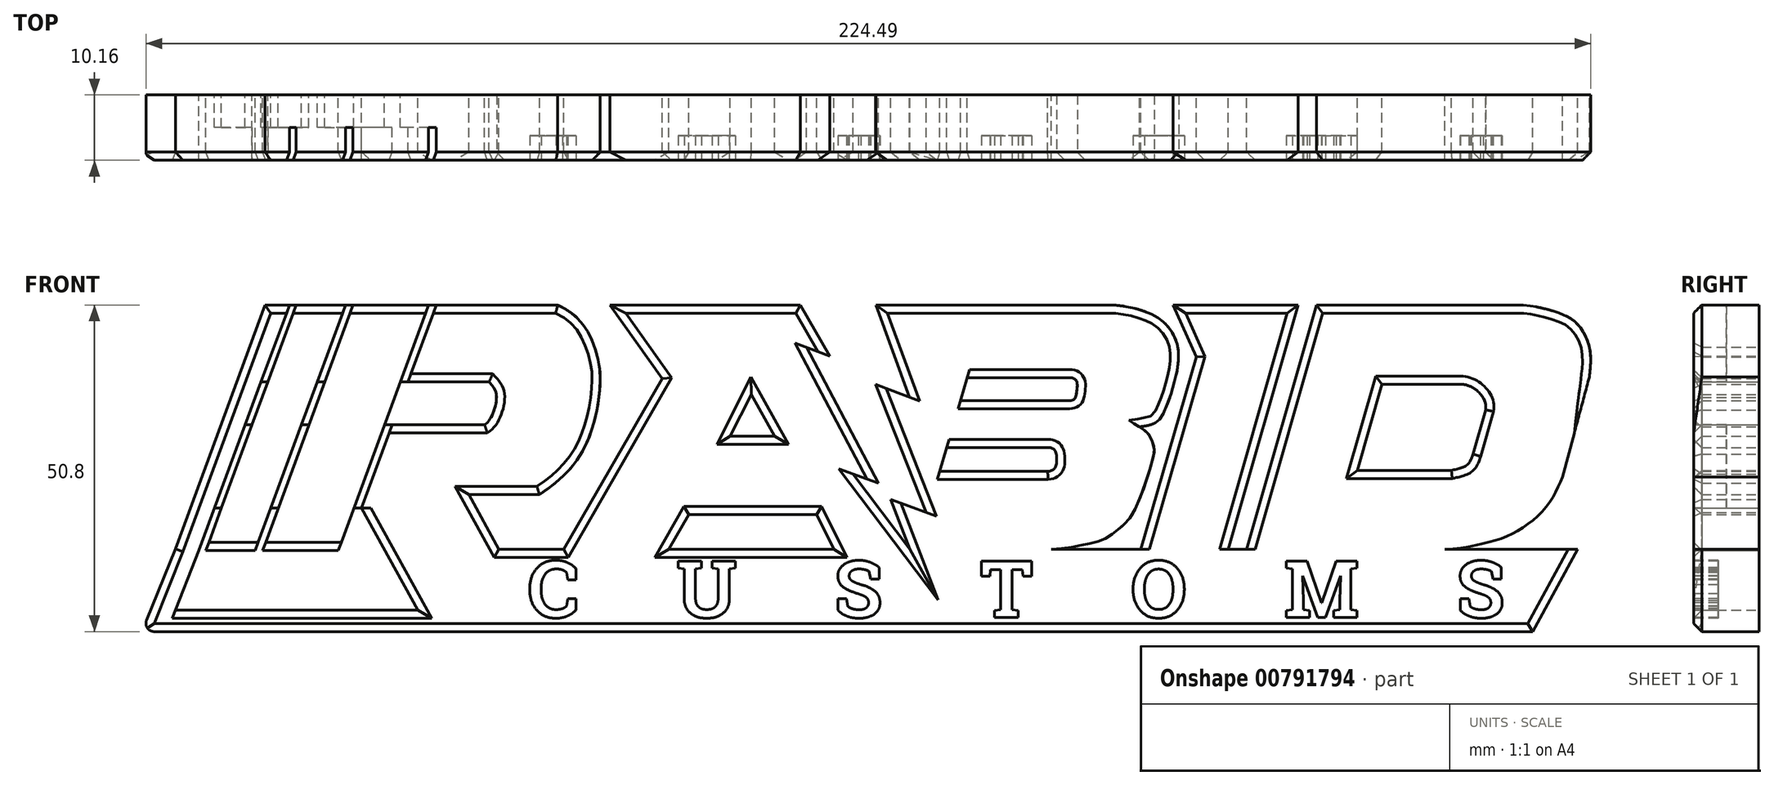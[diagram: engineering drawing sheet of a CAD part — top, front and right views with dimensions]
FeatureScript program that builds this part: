
annotation { "Feature Type Name" : "Feature", "Feature Type Description" : "" }
export const myFeature = defineFeature(function(context is Context, id is Id, definition is map)
    precondition{}
    {
        {
            var Q0;
            Q0=qCreatedBy(makeId("Front.planeOp"),FACE);
            var sketch = newSketch(context, id + "F0", { "sketchPlane" : qUnion([Q0])});
            skLineSegment(sketch, "E0", {"start": v(44.45, 18.23) * mm, "end": v(13.33, 18.23) * mm});
            skLineSegment(sketch, "E1", {"start": v(-163.98, -19.69) * mm, "end": v(-150.03, 18.23) * mm});
            skLineSegment(sketch, "E2", {"start": v(-138.67, -19.93) * mm, "end": v(-150.42, -19.93) * mm});
            skLineSegment(sketch, "E3", {"start": v(-150.69, 6.26) * mm, "end": v(-153.14, -0.4) * mm});
            skLineSegment(sketch, "E4", {"start": v(-159.23, -19.93) * mm, "end": v(-156.81, -13.36) * mm});
            skLineSegment(sketch, "E5", {"start": v(-141.94, 6.26) * mm, "end": v(-144.39, -0.4) * mm});
            skLineSegment(sketch, "E6", {"start": v(-150.42, -19.93) * mm, "end": v(-148, -13.36) * mm});
            skLineSegment(sketch, "E7", {"start": v(-129.04, 6.26) * mm, "end": v(-131.49, -0.4) * mm});
            skLineSegment(sketch, "E8", {"start": v(-127.97, 6.26) * mm, "end": v(-115.24, 6.26) * mm});
            skLineSegment(sketch, "E9", {"start": v(-115.92, -0.4) * mm, "end": v(-130.28, -0.4) * mm});
            skLineSegment(sketch, "E10", {"start": v(-135.05, -13.36) * mm, "end": v(-126.3, -29.24) * mm});
            skLineSegment(sketch, "E11", {"start": v(-124.47, -32.57) * mm, "end": v(-110.55, -32.57) * mm});
            skLineSegment(sketch, "E12", {"start": v(-110.55, -32.57) * mm, "end": v(-103.65, -19.74) * mm});
            skLineSegment(sketch, "E13", {"start": v(-103.65, -19.74) * mm, "end": v(-113.7, -19.74) * mm});
            skLineSegment(sketch, "E14", {"start": v(-113.7, -19.74) * mm, "end": v(-118.36, -11.28) * mm});
            skLineSegment(sketch, "E15", {"start": v(-118.36, -11.28) * mm, "end": v(-107.38, -11.28) * mm});
            skLineSegment(sketch, "E16", {"start": v(-103.65, -19.74) * mm, "end": v(-87.29, -19.74) * mm});
            skLineSegment(sketch, "E17", {"start": v(-96.42, 18.23) * mm, "end": v(-88.35, 6.81) * mm});
            skLineSegment(sketch, "E18", {"start": v(-88.35, 6.81) * mm, "end": v(-103.65, -19.74) * mm});
            skLineSegment(sketch, "E19", {"start": v(-87.29, -19.74) * mm, "end": v(-84.2, -14.4) * mm});
            skLineSegment(sketch, "E20", {"start": v(-84.2, -14.4) * mm, "end": v(-64.33, -14.4) * mm});
            skLineSegment(sketch, "E21", {"start": v(-64.33, -14.4) * mm, "end": v(-61.66, -19.74) * mm});
            skLineSegment(sketch, "E22", {"start": v(-66.84, 18.23) * mm, "end": v(-62.3, 10.3) * mm});
            skLineSegment(sketch, "E23", {"start": v(-62.3, 10.3) * mm, "end": v(-65.92, 11.65) * mm});
            skLineSegment(sketch, "E24", {"start": v(-65.92, 11.65) * mm, "end": v(-54.7, -9.5) * mm});
            skLineSegment(sketch, "E25", {"start": v(-54.7, -9.5) * mm, "end": v(-58.68, -8.06) * mm});
            skLineSegment(sketch, "E26", {"start": v(-58.68, -8.06) * mm, "end": v(-49.86, -19.74) * mm});
            skLineSegment(sketch, "E27", {"start": v(-70.89, -2.18) * mm, "end": v(-77.76, -2.18) * mm});
            skLineSegment(sketch, "E28", {"start": v(-77.76, -2.18) * mm, "end": v(-74.5, 4.32) * mm});
            skLineSegment(sketch, "E29", {"start": v(-74.5, 4.32) * mm, "end": v(-70.89, -2.18) * mm});
            skLineSegment(sketch, "E30", {"start": v(-55.14, 18.23) * mm, "end": v(-49.92, 3.87) * mm});
            skLineSegment(sketch, "E31", {"start": v(-49.92, 3.87) * mm, "end": v(-55.16, 5.86) * mm});
            skLineSegment(sketch, "E32", {"start": v(-55.16, 5.86) * mm, "end": v(-47.3, -14.02) * mm});
            skLineSegment(sketch, "E33", {"start": v(-47.3, -14.02) * mm, "end": v(-52.8, -12.04) * mm});
            skLineSegment(sketch, "E34", {"start": v(-52.8, -12.04) * mm, "end": v(-49.86, -19.74) * mm});
            skLineSegment(sketch, "E35", {"start": v(-40.97, 6.88) * mm, "end": v(-42, 3.36) * mm});
            skLineSegment(sketch, "E36", {"start": v(-45.2, -7.65) * mm, "end": v(-28.43, -7.65) * mm});
            skLineSegment(sketch, "E37", {"start": v(-44.14, -3.97) * mm, "end": v(-28.03, -3.97) * mm});
            skLineSegment(sketch, "E38", {"start": v(-40.97, 6.88) * mm, "end": v(-24.6, 6.88) * mm});
            skLineSegment(sketch, "E39", {"start": v(-42, 3.36) * mm, "end": v(-25, 3.36) * mm});
            skLineSegment(sketch, "E40", {"start": v(-8.93, 18.23) * mm, "end": v(-5.34, 10.12) * mm});
            skLineSegment(sketch, "E41", {"start": v(-5.34, 10.12) * mm, "end": v(-13.99, -19.74) * mm});
            skLineSegment(sketch, "E42", {"start": v(10.46, 18.23) * mm, "end": v(-0.4, -19.74) * mm});
            skLineSegment(sketch, "E43", {"start": v(13.33, 18.23) * mm, "end": v(2.47, -19.74) * mm});
            skLineSegment(sketch, "E44", {"start": v(35.81, 5.9) * mm, "end": v(23.48, 5.9) * mm});
            skLineSegment(sketch, "E45", {"start": v(23.48, 5.9) * mm, "end": v(19.66, -7.49) * mm});
            skLineSegment(sketch, "E46", {"start": v(19.66, -7.49) * mm, "end": v(34.3, -7.49) * mm});
            skLineSegment(sketch, "E47", {"start": v(39.6, 1.92) * mm, "end": v(37.65, -4.94) * mm});
            skFitSpline(sketch, "E48", {"points": [v(55.73, 7.05) * mm, v(55.73, 11.7) * mm, v(53.74, 15.4) * mm, v(50.9, 17) * mm, v(44.45, 18.23) * mm], "startDerivative": vector(2.3, 18.78) * mm, "endDerivative": vector(-24.45, 0) * mm});
            skLineSegment(sketch, "E49", {"start": v(55.73, 7.05) * mm, "end": v(51.56, -8.5) * mm});
            skFitSpline(sketch, "E50", {"points": [v(-14.17, -0.73) * mm, v(-12.02, -0.26) * mm, v(-10.54, 1.23) * mm, v(-8.14, 9.39) * mm, v(-8.72, 13.21) * mm, v(-10.35, 15.5) * mm, v(-13.7, 17.35) * mm, v(-18.93, 18.23) * mm], "startDerivative": vector(20.2, 3.41) * mm, "endDerivative": vector(-28.09, 0) * mm});
            skFitSpline(sketch, "E51", {"points": [v(-14.17, -0.73) * mm, v(-12.8, -1.84) * mm, v(-11.95, -3.81) * mm, v(-12.1, -5.72) * mm, v(-14.99, -13.75) * mm, v(-17.24, -16.5) * mm, v(-19.85, -18.27) * mm, v(-23.1, -19.11) * mm, v(-27.89, -19.74) * mm], "startDerivative": vector(16.43, -10.07) * mm, "endDerivative": vector(-33.98, 0) * mm});
            skFitSpline(sketch, "E52", {"points": [v(-24.6, 6.88) * mm, v(-24.2, 6.68) * mm, v(-23.87, 6.14) * mm, v(-24.05, 4.06) * mm, v(-24.29, 3.61) * mm, v(-25, 3.36) * mm], "startDerivative": vector(3.09, 0) * mm, "endDerivative": vector(-4.49, 0) * mm});
            skFitSpline(sketch, "E53", {"points": [v(-28.03, -3.97) * mm, v(-27.5, -4.2) * mm, v(-27.12, -4.85) * mm, v(-27.1, -6.65) * mm, v(-27.44, -7.25) * mm, v(-28.43, -7.65) * mm], "startDerivative": vector(3.73, 0) * mm, "endDerivative": vector(-8.7, -0.89) * mm});
            skFitSpline(sketch, "E54", {"points": [v(-104.57, 18.23) * mm, v(-101.7, 16.39) * mm, v(-99.55, 13.37) * mm, v(-98.04, 8.28) * mm, v(-98.33, 2.83) * mm, v(-99.98, -3.05) * mm, v(-103.2, -7.86) * mm, v(-107.38, -11.28) * mm], "startDerivative": vector(25.95, -13.02) * mm, "endDerivative": vector(-29.28, -21.25) * mm});
            skFitSpline(sketch, "E55", {"points": [v(35.81, 5.9) * mm, v(37.17, 5.6) * mm, v(38.23, 4.97) * mm, v(39.07, 4.03) * mm, v(39.6, 1.92) * mm], "startDerivative": vector(5.58, 0) * mm, "endDerivative": vector(-1.33, -10.82) * mm});
            skFitSpline(sketch, "E56", {"points": [v(34.3, -7.49) * mm, v(35.48, -7.2) * mm, v(36.57, -6.77) * mm, v(37.26, -5.96) * mm, v(37.65, -4.94) * mm], "startDerivative": vector(4.57, 1.01) * mm, "endDerivative": vector(1.33, 4.26) * mm});
            skLineSegment(sketch, "E57.trimOffspring", {"start": v(-146.28, 18.23) * mm, "end": v(-150.03, 18.23) * mm});
            skLineSegment(sketch, "E58.trimOffspring", {"start": v(-137.53, 18.23) * mm, "end": v(-145.19, 18.23) * mm});
            skLineSegment(sketch, "E59.trimOffspring", {"start": v(-124.63, 18.23) * mm, "end": v(-136.37, 18.23) * mm});
            skLineSegment(sketch, "E60.trimOffspring", {"start": v(-104.57, 18.23) * mm, "end": v(-123.56, 18.23) * mm});
            skLineSegment(sketch, "E61.trimOffspring", {"start": v(-151.57, -19.93) * mm, "end": v(-159.23, -19.93) * mm});
            skLineSegment(sketch, "E62.trimOffspring", {"start": v(-61.66, -19.74) * mm, "end": v(-49.86, -19.74) * mm});
            skLineSegment(sketch, "E63.trimOffspring", {"start": v(-49.86, -19.74) * mm, "end": v(-27.89, -19.74) * mm});
            skLineSegment(sketch, "E64.trimOffspring", {"start": v(-66.84, 18.23) * mm, "end": v(-96.42, 18.23) * mm});
            skLineSegment(sketch, "E65.trimOffspring", {"start": v(-44.14, -3.97) * mm, "end": v(-45.2, -7.65) * mm});
            skLineSegment(sketch, "E66.trimOffspring", {"start": v(-18.93, 18.23) * mm, "end": v(-55.14, 18.23) * mm});
            skLineSegment(sketch, "E67.trimOffspring", {"start": v(-13.99, -19.74) * mm, "end": v(-0.4, -19.74) * mm});
            skLineSegment(sketch, "E68.trimOffspring", {"start": v(2.47, -19.74) * mm, "end": v(33.3, -19.74) * mm});
            skLineSegment(sketch, "E69.trimOffspring", {"start": v(10.46, 18.23) * mm, "end": v(-8.93, 18.23) * mm});
            skFitSpline(sketch, "E70", {"points": [v(51.56, -8.5) * mm, v(50.36, -11.15) * mm, v(48.41, -13.9) * mm, v(45.57, -16.27) * mm, v(42.49, -17.92) * mm, v(38.84, -18.97) * mm, v(33.3, -19.74) * mm], "startDerivative": vector(-7.47, -18.05) * mm, "endDerivative": vector(-28.9, 0) * mm});
            skFitSpline(sketch, "E71", {"points": [v(-115.24, 6.26) * mm, v(-114.2, 4.72) * mm, v(-114.26, 2.54) * mm, v(-115.24, 0.25) * mm, v(-115.92, -0.4) * mm], "startDerivative": vector(5.02, -5.67) * mm, "endDerivative": vector(-3.78, -2.78) * mm});
            skLineSegment(sketch, "E72", {"start": v(-87.29, -19.74) * mm, "end": v(-61.66, -19.74) * mm});
            skLineSegment(sketch, "E73", {"start": v(-27.89, -19.74) * mm, "end": v(-13.99, -19.74) * mm});
            skLineSegment(sketch, "E74", {"start": v(-0.4, -19.74) * mm, "end": v(2.47, -19.74) * mm});
            skLineSegment(sketch, "E75", {"start": v(27.98, -32.57) * mm, "end": v(-110.55, -32.57) * mm});
            skLineSegment(sketch, "E76", {"start": v(27.98, -32.57) * mm, "end": v(46.92, -32.57) * mm});
            skLineSegment(sketch, "E77", {"start": v(46.92, -32.57) * mm, "end": v(53.92, -19.74) * mm});
            skLineSegment(sketch, "E78", {"start": v(33.3, -19.74) * mm, "end": v(53.92, -19.74) * mm});
            skLineSegment(sketch, "E79", {"start": v(-123.56, 18.23) * mm, "end": v(-124.63, 18.23) * mm});
            skLineSegment(sketch, "E80", {"start": v(-136.37, 18.23) * mm, "end": v(-137.53, 18.23) * mm});
            skLineSegment(sketch, "E81", {"start": v(-127.97, 6.26) * mm, "end": v(-129.04, 6.26) * mm});
            skLineSegment(sketch, "E82", {"start": v(-130.28, -0.4) * mm, "end": v(-131.49, -0.4) * mm});
            skLineSegment(sketch, "E83", {"start": v(-145.19, 18.23) * mm, "end": v(-146.28, 18.23) * mm});
            skLineSegment(sketch, "E84", {"start": v(-140.78, 6.26) * mm, "end": v(-141.94, 6.26) * mm});
            skLineSegment(sketch, "E85", {"start": v(-149.6, 6.26) * mm, "end": v(-150.69, 6.26) * mm});
            skLineSegment(sketch, "E86", {"start": v(-143.23, -0.4) * mm, "end": v(-144.39, -0.4) * mm});
            skLineSegment(sketch, "E87", {"start": v(-152.05, -0.4) * mm, "end": v(-153.14, -0.4) * mm});
            skLineSegment(sketch, "E88", {"start": v(-135.05, -13.36) * mm, "end": v(-136.25, -13.36) * mm});
            skLineSegment(sketch, "E89", {"start": v(-148, -13.36) * mm, "end": v(-149.15, -13.36) * mm});
            skLineSegment(sketch, "E90", {"start": v(-156.81, -13.36) * mm, "end": v(-157.9, -13.36) * mm});
            skLineSegment(sketch, "E91", {"start": v(-163.98, -19.69) * mm, "end": v(-168.88, -31.87) * mm});
            skLineSegment(sketch, "E92", {"start": v(-168.4, -32.57) * mm, "end": v(-124.47, -32.57) * mm});
            skLineSegment(sketch, "E93", {"start": v(-160.32, -19.93) * mm, "end": v(-163.98, -29.24) * mm});
            skLineSegment(sketch, "E94", {"start": v(-163.98, -29.24) * mm, "end": v(-126.3, -29.24) * mm});
            skLineSegment(sketch, "E95.trimOffspring", {"start": v(-152.05, -0.4) * mm, "end": v(-149.6, 6.26) * mm});
            skLineSegment(sketch, "E96.trimOffspring", {"start": v(-157.9, -13.36) * mm, "end": v(-160.32, -19.93) * mm});
            skLineSegment(sketch, "E97.trimOffspring", {"start": v(-149.15, -13.36) * mm, "end": v(-151.57, -19.93) * mm});
            skLineSegment(sketch, "E98.trimOffspring", {"start": v(-143.23, -0.4) * mm, "end": v(-140.78, 6.26) * mm});
            skLineSegment(sketch, "E99.trimOffspring", {"start": v(-136.25, -13.36) * mm, "end": v(-138.67, -19.93) * mm});
            skLineSegment(sketch, "E100", {"start": v(-168.88, -31.87) * mm, "end": v(-169.16, -32.57) * mm});
            skLineSegment(sketch, "E101", {"start": v(-169.16, -32.57) * mm, "end": v(-168.4, -32.57) * mm});
            skSolve(sketch);
        }
        {
            var Q0;
            Q0=qSketchRegion(id+"F0",true);
            extrude(context, id + "F1", {"entities" : qUnion([Q0]), "depth" : 10.16 * mm, "offsetDistance" : 25.4 * mm});
        }
        {
            var Q0;
            {var subQ0=sQuery(id+"F0.wireOp",EDGE,"E28");var subQ1=sQuery(id+"F0.wireOp",EDGE,"E27");var subQ2=sQuery(id+"F0.wireOp",EDGE,"E25");var subQ3=sQuery(id+"F0.wireOp",EDGE,"E22");var subQ4=sQuery(id+"F0.wireOp",EDGE,"E21");var subQ5=sQuery(id+"F0.wireOp",EDGE,"E20");var subQ6=sQuery(id+"F0.wireOp",EDGE,"E19");var subQ7=sQuery(id+"F0.wireOp",EDGE,"E18");var subQ8=sQuery(id+"F0.wireOp",EDGE,"E17");var subQ9=sQuery(id+"F0.wireOp",EDGE,"E15");var subQ10=sQuery(id+"F0.wireOp",EDGE,"E14");var subQ11=sQuery(id+"F0.wireOp",EDGE,"E13");var subQ12=sQuery(id+"F0.wireOp",EDGE,"E76");var subQ13=sQuery(id+"F0.wireOp",EDGE,"E75");var subQ14=sQuery(id+"F0.wireOp",EDGE,"E11");var subQ15=sQuery(id+"F0.wireOp",EDGE,"E10");var subQ16=sQuery(id+"F0.wireOp",EDGE,"E82");var subQ17=sQuery(id+"F0.wireOp",EDGE,"E9");var subQ18=sQuery(id+"F0.wireOp",EDGE,"E81");var subQ19=sQuery(id+"F0.wireOp",EDGE,"E8");var subQ20=sQuery(id+"F0.wireOp",EDGE,"E7");var subQ21=sQuery(id+"F0.wireOp",EDGE,"E2");var subQ22=sQuery(id+"F0.wireOp",EDGE,"E88");var subQ23=sQuery(id+"F0.wireOp",EDGE,"E84");var subQ24=sQuery(id+"F0.wireOp",EDGE,"E6");var subQ25=sQuery(id+"F0.wireOp",EDGE,"E86");var subQ26=sQuery(id+"F0.wireOp",EDGE,"E89");var subQ27=sQuery(id+"F0.wireOp",EDGE,"E61.trimOffspring");var subQ28=sQuery(id+"F0.wireOp",EDGE,"E5");var subQ29=sQuery(id+"F0.wireOp",EDGE,"E85");var subQ30=sQuery(id+"F0.wireOp",EDGE,"E4");var subQ31=sQuery(id+"F0.wireOp",EDGE,"E87");var subQ32=sQuery(id+"F0.wireOp",EDGE,"E90");var subQ33=sQuery(id+"F0.wireOp",EDGE,"f4ebd289-e4e5-4d37-ab03-dc2c71f6bb5f.trimOffspring");var subQ34=sQuery(id+"F0.wireOp",EDGE,"E3");var subQ35=sQuery(id+"F0.wireOp",EDGE,"E1");var subQ36=sQuery(id+"F0.wireOp",EDGE,"E0");var subQ37=sQuery(id+"F0.wireOp",EDGE,"E78");var subQ38=sQuery(id+"F0.wireOp",EDGE,"E77");var subQ39=sQuery(id+"F0.wireOp",EDGE,"E73");var subQ40=sQuery(id+"F0.wireOp",EDGE,"E72");var subQ41=sQuery(id+"F0.wireOp",EDGE,"E71");var subQ42=sQuery(id+"F0.wireOp",EDGE,"E70");var subQ43=sQuery(id+"F0.wireOp",EDGE,"E69.trimOffspring");var subQ44=sQuery(id+"F0.wireOp",EDGE,"E66.trimOffspring");var subQ45=sQuery(id+"F0.wireOp",EDGE,"E65.trimOffspring");var subQ46=sQuery(id+"F0.wireOp",EDGE,"E46");var subQ47=sQuery(id+"F0.wireOp",EDGE,"E74");var subQ48=sQuery(id+"F0.wireOp",EDGE,"E45");var subQ49=sQuery(id+"F0.wireOp",EDGE,"E43");var subQ50=sQuery(id+"F0.wireOp",EDGE,"E48");var subQ51=sQuery(id+"F0.wireOp",EDGE,"E26");var subQ52=sQuery(id+"F0.wireOp",EDGE,"E47");var subQ53=sQuery(id+"F0.wireOp",EDGE,"E44");var subQ54=sQuery(id+"F0.wireOp",EDGE,"E53");var subQ55=sQuery(id+"F0.wireOp",EDGE,"E39");var subQ56=sQuery(id+"F0.wireOp",EDGE,"E38");var subQ57=sQuery(id+"F0.wireOp",EDGE,"E30");var subQ58=sQuery(id+"F0.wireOp",EDGE,"E29");var subQ59=sQuery(id+"F0.wireOp",EDGE,"E31");var subQ60=sQuery(id+"F0.wireOp",EDGE,"E49");var subQ61=sQuery(id+"F0.wireOp",EDGE,"E42");var subQ62=sQuery(id+"F0.wireOp",EDGE,"E37");var subQ63=sQuery(id+"F0.wireOp",EDGE,"E32");var subQ64=sQuery(id+"F0.wireOp",EDGE,"E33");var subQ65=sQuery(id+"F0.wireOp",EDGE,"E34");var subQ66=sQuery(id+"F0.wireOp",EDGE,"E35");var subQ67=sQuery(id+"F0.wireOp",EDGE,"E36");var subQ68=sQuery(id+"F0.wireOp",EDGE,"E50");var subQ69=sQuery(id+"F0.wireOp",EDGE,"E51");var subQ70=sQuery(id+"F0.wireOp",EDGE,"E52");var subQ71=sQuery(id+"F0.wireOp",EDGE,"E54");var subQ72=sQuery(id+"F0.wireOp",EDGE,"E23");var subQ73=sQuery(id+"F0.wireOp",EDGE,"E55");var subQ74=sQuery(id+"F0.wireOp",EDGE,"E24");var subQ75=sQuery(id+"F0.wireOp",EDGE,"E56");var subQ76=sQuery(id+"F0.wireOp",EDGE,"E83");var subQ77=sQuery(id+"F0.wireOp",EDGE,"E80");var subQ78=sQuery(id+"F0.wireOp",EDGE,"E79");var subQ79=sQuery(id+"F0.wireOp",EDGE,"E60.trimOffspring");var subQ80=sQuery(id+"F0.wireOp",EDGE,"E59.trimOffspring");var subQ81=sQuery(id+"F0.wireOp",EDGE,"E58.trimOffspring");var subQ82=sQuery(id+"F0.wireOp",EDGE,"E57.trimOffspring");var subQ83=sQuery(id+"F0.wireOp",EDGE,"E64.trimOffspring");var subQ84=sQuery(id+"F0.wireOp",EDGE,"E40");var subQ85=sQuery(id+"F0.wireOp",EDGE,"E41");Q0=makeQuery(id+"F5.boolean.opBoolean","SPLIT",FACE,{"disambiguationData":[TD([makeQuery(id+"F1.opExtrude","SWEPT_FACE",FACE,{"disambiguationData":[OSD([subQ36])]})])],"derivedFrom":makeQuery(id+"F1.opExtrude","CAP_FACE",FACE,{"disambiguationData":[OSD([subQ36,subQ35,subQ21,subQ34,subQ30,subQ28,subQ24,subQ20,subQ19,subQ17,subQ15,subQ14,subQ11,subQ10,subQ9,subQ8,subQ7,subQ6,subQ5,subQ4,subQ3,subQ72,subQ74,subQ2,subQ51,subQ1,subQ0,subQ58,subQ57,subQ59,subQ63,subQ64,subQ65,subQ66,subQ67,subQ62,subQ56,subQ55,subQ84,subQ85,subQ61,subQ49,subQ53,subQ48,subQ46,subQ52,subQ50,subQ60,subQ68,subQ69,subQ70,subQ54,subQ71,subQ73,subQ75,subQ82,subQ81,subQ80,subQ79,subQ27,subQ33,subQ83,subQ45,subQ44,subQ43,subQ42,subQ41,subQ40,subQ39,subQ47,subQ13,subQ12,subQ38,subQ37,subQ78,subQ77,subQ18,subQ16,subQ76,subQ23,subQ29,subQ25,subQ31,subQ22,subQ26,subQ32])],"isStart":false})});}
            var sketch = newSketch(context, id + "F2", { "sketchPlane" : qUnion([Q0])});
            skLineSegment(sketch, "E102", {"start": v(-159.23, -19.93) * mm, "end": v(-145.22, 18.23) * mm});
            skLineSegment(sketch, "E103", {"start": v(-145.22, 18.23) * mm, "end": v(-146.23, 18.23) * mm});
            skLineSegment(sketch, "E104", {"start": v(-146.23, 18.23) * mm, "end": v(-150.69, 6.26) * mm});
            skLineSegment(sketch, "E105", {"start": v(-159.23, -19.93) * mm, "end": v(-150.42, -19.93) * mm});
            skLineSegment(sketch, "E106", {"start": v(-150.42, -19.93) * mm, "end": v(-136.37, 18.23) * mm});
            skLineSegment(sketch, "E107", {"start": v(-136.37, 18.23) * mm, "end": v(-137.53, 18.23) * mm});
            skLineSegment(sketch, "E108", {"start": v(-138.67, -19.93) * mm, "end": v(-124.63, 18.23) * mm});
            skLineSegment(sketch, "E109", {"start": v(-124.63, 18.23) * mm, "end": v(-123.44, 18.23) * mm});
            skLineSegment(sketch, "E110", {"start": v(-123.44, 18.23) * mm, "end": v(-137.48, -19.93) * mm});
            skLineSegment(sketch, "E111", {"start": v(-137.48, -19.93) * mm, "end": v(-138.67, -19.93) * mm});
            skLineSegment(sketch, "E112", {"start": v(-137.53, 18.23) * mm, "end": v(-151.57, -19.93) * mm});
            skLineSegment(sketch, "E113", {"start": v(-151.57, -19.93) * mm, "end": v(-150.42, -19.93) * mm});
            skLineSegment(sketch, "E114", {"start": v(-150.69, 6.26) * mm, "end": v(-160.32, -19.93) * mm});
            skLineSegment(sketch, "E115", {"start": v(-160.32, -19.93) * mm, "end": v(-159.23, -19.93) * mm});
            skSolve(sketch);
        }
        {
            var Q0;
            Q0=qSketchRegion(id+"F2",true);
            extrude(context, id + "F3", {"entities" : qUnion([Q0]), "operationType" : NewBodyOperationType.REMOVE, "oppositeDirection" : true, "depth" : 5.08 * mm, "offsetDistance" : 25.4 * mm});
        }
        {
            var Q0;
            Q0=makeQuery(id+"F1.opExtrude","CAP_FACE",FACE,{"disambiguationData":[OSD([sQuery(id+"F0.wireOp",EDGE,"E0"),sQuery(id+"F0.wireOp",EDGE,"b24fb574-62dd-4393-ad03-bf6b0ade210b"),sQuery(id+"F0.wireOp",EDGE,"E8"),sQuery(id+"F0.wireOp",EDGE,"E9"),sQuery(id+"F0.wireOp",EDGE,"1671c6c2-1b25-43a6-b499-dadc8ae943b3"),sQuery(id+"F0.wireOp",EDGE,"E10"),sQuery(id+"F0.wireOp",EDGE,"E11"),sQuery(id+"F0.wireOp",EDGE,"E13"),sQuery(id+"F0.wireOp",EDGE,"E14"),sQuery(id+"F0.wireOp",EDGE,"E15"),sQuery(id+"F0.wireOp",EDGE,"E17"),sQuery(id+"F0.wireOp",EDGE,"E18"),sQuery(id+"F0.wireOp",EDGE,"E19"),sQuery(id+"F0.wireOp",EDGE,"E20"),sQuery(id+"F0.wireOp",EDGE,"E21"),sQuery(id+"F0.wireOp",EDGE,"E22"),sQuery(id+"F0.wireOp",EDGE,"E23"),sQuery(id+"F0.wireOp",EDGE,"E24"),sQuery(id+"F0.wireOp",EDGE,"E25"),sQuery(id+"F0.wireOp",EDGE,"E26"),sQuery(id+"F0.wireOp",EDGE,"E27"),sQuery(id+"F0.wireOp",EDGE,"E28"),sQuery(id+"F0.wireOp",EDGE,"E29"),sQuery(id+"F0.wireOp",EDGE,"E30"),sQuery(id+"F0.wireOp",EDGE,"E31"),sQuery(id+"F0.wireOp",EDGE,"E32"),sQuery(id+"F0.wireOp",EDGE,"E33"),sQuery(id+"F0.wireOp",EDGE,"E34"),sQuery(id+"F0.wireOp",EDGE,"E35"),sQuery(id+"F0.wireOp",EDGE,"E36"),sQuery(id+"F0.wireOp",EDGE,"E37"),sQuery(id+"F0.wireOp",EDGE,"E38"),sQuery(id+"F0.wireOp",EDGE,"E39"),sQuery(id+"F0.wireOp",EDGE,"E40"),sQuery(id+"F0.wireOp",EDGE,"E41"),sQuery(id+"F0.wireOp",EDGE,"E42"),sQuery(id+"F0.wireOp",EDGE,"E43"),sQuery(id+"F0.wireOp",EDGE,"E44"),sQuery(id+"F0.wireOp",EDGE,"E45"),sQuery(id+"F0.wireOp",EDGE,"E46"),sQuery(id+"F0.wireOp",EDGE,"E47"),sQuery(id+"F0.wireOp",EDGE,"E48"),sQuery(id+"F0.wireOp",EDGE,"E49"),sQuery(id+"F0.wireOp",EDGE,"E50"),sQuery(id+"F0.wireOp",EDGE,"E51"),sQuery(id+"F0.wireOp",EDGE,"E52"),sQuery(id+"F0.wireOp",EDGE,"E53"),sQuery(id+"F0.wireOp",EDGE,"E54"),sQuery(id+"F0.wireOp",EDGE,"E55"),sQuery(id+"F0.wireOp",EDGE,"E56"),sQuery(id+"F0.wireOp",EDGE,"E60.trimOffspring"),sQuery(id+"F0.wireOp",EDGE,"E64.trimOffspring"),sQuery(id+"F0.wireOp",EDGE,"E65.trimOffspring"),sQuery(id+"F0.wireOp",EDGE,"E66.trimOffspring"),sQuery(id+"F0.wireOp",EDGE,"E69.trimOffspring"),sQuery(id+"F0.wireOp",EDGE,"E70"),sQuery(id+"F0.wireOp",EDGE,"E71"),sQuery(id+"F0.wireOp",EDGE,"E72"),sQuery(id+"F0.wireOp",EDGE,"E73"),sQuery(id+"F0.wireOp",EDGE,"E74"),sQuery(id+"F0.wireOp",EDGE,"ISSC0bJT-fq30-P4vY-vGbu-V4KtggNEUtfu"),sQuery(id+"F0.wireOp",EDGE,"E75")])],"isStart":false});
            var sketch = newSketch(context, id + "F4", { "sketchPlane" : qUnion([Q0])});
            skText(sketch, "E116", { "text": "C     U     S     T     O     M     S", "fontName": "RobotoSlab-Bold.ttf"});
            const initialGuessF4  = {"E116": [-0.10922, -0.03037, 1, 0, 0.00889]};
            skSetInitialGuess(sketch, initialGuessF4);
            skSolve(sketch);
        }
        {
            var Q0;
            Q0=qSketchRegion(id+"F4",true);
            extrude(context, id + "F5", {"entities" : qUnion([Q0]), "operationType" : NewBodyOperationType.REMOVE, "oppositeDirection" : true, "depth" : 3.8 * mm, "offsetDistance" : 25.4 * mm});
        }
        {
            var Q0;
            {var subQ0=sQuery(id+"F0.wireOp",EDGE,"E83");var subQ1=sQuery(id+"F0.wireOp",EDGE,"E80");var subQ2=sQuery(id+"F0.wireOp",EDGE,"E79");var subQ3=sQuery(id+"F0.wireOp",EDGE,"E60.trimOffspring");var subQ4=sQuery(id+"F0.wireOp",EDGE,"E59.trimOffspring");var subQ5=sQuery(id+"F0.wireOp",EDGE,"E58.trimOffspring");var subQ6=sQuery(id+"F0.wireOp",EDGE,"E57.trimOffspring");var subQ7=sQuery(id+"F0.wireOp",EDGE,"E1");Q0=makeQuery(id+"F3.boolean.opBoolean","SPLIT",EDGE,{"disambiguationData":[TD([makeQuery(id+"F1.opExtrude","SWEPT_FACE",FACE,{"disambiguationData":[OSD([subQ7])]})])],"derivedFrom":makeQuery(id+"F1.opExtrude","CAP_EDGE",EDGE,{"disambiguationData":[OSD([subQ6,subQ5,subQ4,subQ3,subQ2,subQ1,subQ0])],"isStart":false})});}
            var Q1;
            {var subQ0=sQuery(id+"F0.wireOp",EDGE,"E83");var subQ1=sQuery(id+"F0.wireOp",EDGE,"E80");var subQ2=sQuery(id+"F0.wireOp",EDGE,"E79");var subQ3=sQuery(id+"F0.wireOp",EDGE,"E60.trimOffspring");var subQ4=sQuery(id+"F0.wireOp",EDGE,"E59.trimOffspring");var subQ5=sQuery(id+"F0.wireOp",EDGE,"E58.trimOffspring");var subQ6=sQuery(id+"F0.wireOp",EDGE,"E57.trimOffspring");Q1=makeQuery(id+"F3.boolean.opBoolean","SPLIT",EDGE,{"disambiguationData":[TD([makeQuery(id+"F3.opExtrude","SWEPT_FACE",FACE,{"disambiguationData":[OSD([sQuery(id+"F2.wireOp",EDGE,"E102")])]})])],"derivedFrom":makeQuery(id+"F1.opExtrude","CAP_EDGE",EDGE,{"disambiguationData":[OSD([subQ6,subQ5,subQ4,subQ3,subQ2,subQ1,subQ0])],"isStart":false})});}
            var Q2;
            {var subQ1=sQuery(id+"F0.wireOp",EDGE,"E6");var subQ3=sQuery(id+"F0.wireOp",EDGE,"E83");var subQ4=sQuery(id+"F0.wireOp",EDGE,"E80");var subQ5=sQuery(id+"F0.wireOp",EDGE,"E79");var subQ6=sQuery(id+"F0.wireOp",EDGE,"E60.trimOffspring");var subQ7=sQuery(id+"F0.wireOp",EDGE,"E59.trimOffspring");var subQ8=sQuery(id+"F0.wireOp",EDGE,"E58.trimOffspring");var subQ9=sQuery(id+"F0.wireOp",EDGE,"E57.trimOffspring");Q2=makeQuery(id+"F3.boolean.opBoolean","SPLIT",EDGE,{"disambiguationData":[TD([makeQuery(id+"F1.opExtrude","SWEPT_FACE",FACE,{"disambiguationData":[OSD([subQ1])]})])],"derivedFrom":makeQuery(id+"F1.opExtrude","CAP_EDGE",EDGE,{"disambiguationData":[OSD([subQ9,subQ8,subQ7,subQ6,subQ5,subQ4,subQ3])],"isStart":false})});}
            var Q3;
            {var subQ0=sQuery(id+"F0.wireOp",EDGE,"E83");var subQ1=sQuery(id+"F0.wireOp",EDGE,"E80");var subQ2=sQuery(id+"F0.wireOp",EDGE,"E79");var subQ3=sQuery(id+"F0.wireOp",EDGE,"E60.trimOffspring");var subQ4=sQuery(id+"F0.wireOp",EDGE,"E59.trimOffspring");var subQ5=sQuery(id+"F0.wireOp",EDGE,"E58.trimOffspring");var subQ6=sQuery(id+"F0.wireOp",EDGE,"E57.trimOffspring");var subQ7=sQuery(id+"F0.wireOp",EDGE,"E54");Q3=makeQuery(id+"F3.boolean.opBoolean","SPLIT",EDGE,{"disambiguationData":[TD([makeQuery(id+"F1.opExtrude","SWEPT_FACE",FACE,{"disambiguationData":[OSD([subQ7])]})])],"derivedFrom":makeQuery(id+"F1.opExtrude","CAP_EDGE",EDGE,{"disambiguationData":[OSD([subQ6,subQ5,subQ4,subQ3,subQ2,subQ1,subQ0])],"isStart":false})});}
            var Q4;
            Q4=makeQuery(id+"F1.opExtrude","CAP_EDGE",EDGE,{"disambiguationData":[OSD([sQuery(id+"F0.wireOp",EDGE,"E54")])],"isStart":false});
            var Q5;
            Q5=makeQuery(id+"F1.opExtrude","CAP_EDGE",EDGE,{"disambiguationData":[OSD([sQuery(id+"F0.wireOp",EDGE,"E8"),sQuery(id+"F0.wireOp",EDGE,"E81")])],"isStart":false});
            var Q6;
            Q6=makeQuery(id+"F1.opExtrude","CAP_EDGE",EDGE,{"disambiguationData":[OSD([sQuery(id+"F0.wireOp",EDGE,"E9"),sQuery(id+"F0.wireOp",EDGE,"E82")])],"isStart":false});
            var Q7;
            Q7=makeQuery(id+"F1.opExtrude","CAP_EDGE",EDGE,{"disambiguationData":[OSD([sQuery(id+"F0.wireOp",EDGE,"E71")])],"isStart":false});
            var Q8;
            Q8=makeQuery(id+"F1.opExtrude","CAP_EDGE",EDGE,{"disambiguationData":[OSD([sQuery(id+"F0.wireOp",EDGE,"E18")])],"isStart":false});
            var Q9;
            Q9=makeQuery(id+"F1.opExtrude","CAP_EDGE",EDGE,{"disambiguationData":[OSD([sQuery(id+"F0.wireOp",EDGE,"E14")])],"isStart":false});
            var Q10;
            Q10=makeQuery(id+"F1.opExtrude","CAP_EDGE",EDGE,{"disambiguationData":[OSD([sQuery(id+"F0.wireOp",EDGE,"E15")])],"isStart":false});
            var Q11;
            Q11=makeQuery(id+"F1.opExtrude","CAP_EDGE",EDGE,{"disambiguationData":[OSD([sQuery(id+"F0.wireOp",EDGE,"E13")])],"isStart":false});
            var Q12;
            Q12=makeQuery(id+"F1.opExtrude","CAP_EDGE",EDGE,{"disambiguationData":[OSD([sQuery(id+"F0.wireOp",EDGE,"E17")])],"isStart":false});
            var Q13;
            Q13=makeQuery(id+"F1.opExtrude","CAP_EDGE",EDGE,{"disambiguationData":[OSD([sQuery(id+"F0.wireOp",EDGE,"E64.trimOffspring")])],"isStart":false});
            var Q14;
            Q14=makeQuery(id+"F1.opExtrude","CAP_EDGE",EDGE,{"disambiguationData":[OSD([sQuery(id+"F0.wireOp",EDGE,"E22")])],"isStart":false});
            var Q15;
            Q15=makeQuery(id+"F1.opExtrude","CAP_EDGE",EDGE,{"disambiguationData":[OSD([sQuery(id+"F0.wireOp",EDGE,"E24")])],"isStart":false});
            var Q16;
            Q16=makeQuery(id+"F1.opExtrude","CAP_EDGE",EDGE,{"disambiguationData":[OSD([sQuery(id+"F0.wireOp",EDGE,"E26")])],"isStart":false});
            var Q17;
            Q17=makeQuery(id+"F1.opExtrude","CAP_EDGE",EDGE,{"disambiguationData":[OSD([sQuery(id+"F0.wireOp",EDGE,"E34")])],"isStart":false});
            var Q18;
            Q18=makeQuery(id+"F1.opExtrude","CAP_EDGE",EDGE,{"disambiguationData":[OSD([sQuery(id+"F0.wireOp",EDGE,"E30")])],"isStart":false});
            var Q19;
            Q19=makeQuery(id+"F1.opExtrude","CAP_EDGE",EDGE,{"disambiguationData":[OSD([sQuery(id+"F0.wireOp",EDGE,"E66.trimOffspring")])],"isStart":false});
            var Q20;
            Q20=makeQuery(id+"F1.opExtrude","CAP_EDGE",EDGE,{"disambiguationData":[OSD([sQuery(id+"F0.wireOp",EDGE,"E41")])],"isStart":false});
            var Q21;
            Q21=makeQuery(id+"F1.opExtrude","CAP_EDGE",EDGE,{"disambiguationData":[OSD([sQuery(id+"F0.wireOp",EDGE,"E40")])],"isStart":false});
            var Q22;
            Q22=makeQuery(id+"F1.opExtrude","CAP_EDGE",EDGE,{"disambiguationData":[OSD([sQuery(id+"F0.wireOp",EDGE,"E69.trimOffspring")])],"isStart":false});
            var Q23;
            Q23=makeQuery(id+"F1.opExtrude","CAP_EDGE",EDGE,{"disambiguationData":[OSD([sQuery(id+"F0.wireOp",EDGE,"E42")])],"isStart":false});
            var Q24;
            Q24=makeQuery(id+"F1.opExtrude","CAP_EDGE",EDGE,{"disambiguationData":[OSD([sQuery(id+"F0.wireOp",EDGE,"E43")])],"isStart":false});
            var Q25;
            Q25=makeQuery(id+"F1.opExtrude","CAP_EDGE",EDGE,{"disambiguationData":[OSD([sQuery(id+"F0.wireOp",EDGE,"E32")])],"isStart":false});
            var Q26;
            Q26=makeQuery(id+"F1.opExtrude","CAP_EDGE",EDGE,{"disambiguationData":[OSD([sQuery(id+"F0.wireOp",EDGE,"E0")])],"isStart":false});
            var Q27;
            Q27=makeQuery(id+"F1.opExtrude","CAP_EDGE",EDGE,{"disambiguationData":[OSD([sQuery(id+"F0.wireOp",EDGE,"E28")])],"isStart":false});
            var Q28;
            Q28=makeQuery(id+"F1.opExtrude","CAP_EDGE",EDGE,{"disambiguationData":[OSD([sQuery(id+"F0.wireOp",EDGE,"E29")])],"isStart":false});
            var Q29;
            Q29=makeQuery(id+"F1.opExtrude","CAP_EDGE",EDGE,{"disambiguationData":[OSD([sQuery(id+"F0.wireOp",EDGE,"E27")])],"isStart":false});
            var Q30;
            Q30=makeQuery(id+"F1.opExtrude","CAP_EDGE",EDGE,{"disambiguationData":[OSD([sQuery(id+"F0.wireOp",EDGE,"E19")])],"isStart":false});
            var Q31;
            Q31=makeQuery(id+"F1.opExtrude","CAP_EDGE",EDGE,{"disambiguationData":[OSD([sQuery(id+"F0.wireOp",EDGE,"E20")])],"isStart":false});
            var Q32;
            Q32=makeQuery(id+"F1.opExtrude","CAP_EDGE",EDGE,{"disambiguationData":[OSD([sQuery(id+"F0.wireOp",EDGE,"E72")])],"isStart":false});
            var Q33;
            Q33=makeQuery(id+"F1.opExtrude","CAP_EDGE",EDGE,{"disambiguationData":[OSD([sQuery(id+"F0.wireOp",EDGE,"E21")])],"isStart":false});
            var Q34;
            Q34=makeQuery(id+"F1.opExtrude","CAP_EDGE",EDGE,{"disambiguationData":[OSD([sQuery(id+"F0.wireOp",EDGE,"E44")])],"isStart":false});
            var Q35;
            Q35=makeQuery(id+"F1.opExtrude","CAP_EDGE",EDGE,{"disambiguationData":[OSD([sQuery(id+"F0.wireOp",EDGE,"E47")])],"isStart":false});
            var Q36;
            Q36=makeQuery(id+"F1.opExtrude","CAP_EDGE",EDGE,{"disambiguationData":[OSD([sQuery(id+"F0.wireOp",EDGE,"E46")])],"isStart":false});
            var Q37;
            Q37=makeQuery(id+"F1.opExtrude","CAP_EDGE",EDGE,{"disambiguationData":[OSD([sQuery(id+"F0.wireOp",EDGE,"E45")])],"isStart":false});
            var Q38;
            Q38=makeQuery(id+"F1.opExtrude","CAP_EDGE",EDGE,{"disambiguationData":[OSD([sQuery(id+"F0.wireOp",EDGE,"E77")])],"isStart":false});
            var Q39;
            Q39=makeQuery(id+"F1.opExtrude","CAP_EDGE",EDGE,{"disambiguationData":[OSD([sQuery(id+"F0.wireOp",EDGE,"E38")])],"isStart":false});
            var Q40;
            Q40=makeQuery(id+"F1.opExtrude","CAP_EDGE",EDGE,{"disambiguationData":[OSD([sQuery(id+"F0.wireOp",EDGE,"E37")])],"isStart":false});
            var Q41;
            Q41=makeQuery(id+"F1.opExtrude","CAP_EDGE",EDGE,{"disambiguationData":[OSD([sQuery(id+"F0.wireOp",EDGE,"E1")])],"isStart":false});
            var Q42;
            Q42=makeQuery(id+"F1.opExtrude","CAP_EDGE",EDGE,{"disambiguationData":[OSD([sQuery(id+"F0.wireOp",EDGE,"E94")])],"isStart":false});
            var Q43;
            Q43=makeQuery(id+"F1.opExtrude","CAP_EDGE",EDGE,{"disambiguationData":[OSD([sQuery(id+"F0.wireOp",EDGE,"E11"),sQuery(id+"F0.wireOp",EDGE,"E75"),sQuery(id+"F0.wireOp",EDGE,"E76"),sQuery(id+"F0.wireOp",EDGE,"E92"),sQuery(id+"F0.wireOp",EDGE,"E101")])],"isStart":false});
            var Q44;
            Q44=makeQuery(id+"F1.opExtrude","CAP_EDGE",EDGE,{"disambiguationData":[OSD([sQuery(id+"F0.wireOp",EDGE,"E36")])],"isStart":false});
            var Q45;
            Q45=makeQuery(id+"F1.opExtrude","CAP_EDGE",EDGE,{"disambiguationData":[OSD([sQuery(id+"F0.wireOp",EDGE,"E10")])],"isStart":false});
            var Q46;
            Q46=makeQuery(id+"F1.opExtrude","CAP_EDGE",EDGE,{"disambiguationData":[OSD([sQuery(id+"F0.wireOp",EDGE,"E2")])],"isStart":false});
            var Q47;
            Q47=makeQuery(id+"F1.opExtrude","CAP_EDGE",EDGE,{"disambiguationData":[OSD([sQuery(id+"F0.wireOp",EDGE,"E61.trimOffspring")])],"isStart":false});
            chamfer(context, id + "F6", {"entities" : qUnion([Q0, Q1, Q2, Q3, Q4, Q5, Q6, Q7, Q8, Q9, Q10, Q11, Q12, Q13, Q14, Q15, Q16, Q17, Q18, Q19, Q20, Q21, Q22, Q23, Q24, Q25, Q26, Q27, Q28, Q29, Q30, Q31, Q32, Q33, Q34, Q35, Q36, Q37, Q38, Q39, Q40, Q41, Q42, Q43, Q44, Q45, Q46, Q47]), "width" : 1.27 * mm, "tangentPropagation" : true});
        }
        {
            var Q0;
            Q0=makeQuery(id+"F1.opExtrude","SWEPT_EDGE",EDGE,{"disambiguationData":[OSD([sQuery(id+"F0.wireOp",EDGE,"E100"),sQuery(id+"F0.wireOp",EDGE,"E101")])]});
            fillet(context, id + "F7", {"entities" : qUnion([Q0]), "radius" : 1.27 * mm, "tangentPropagation" : true, "allowEdgeOverflow" : false});
        }
    });
